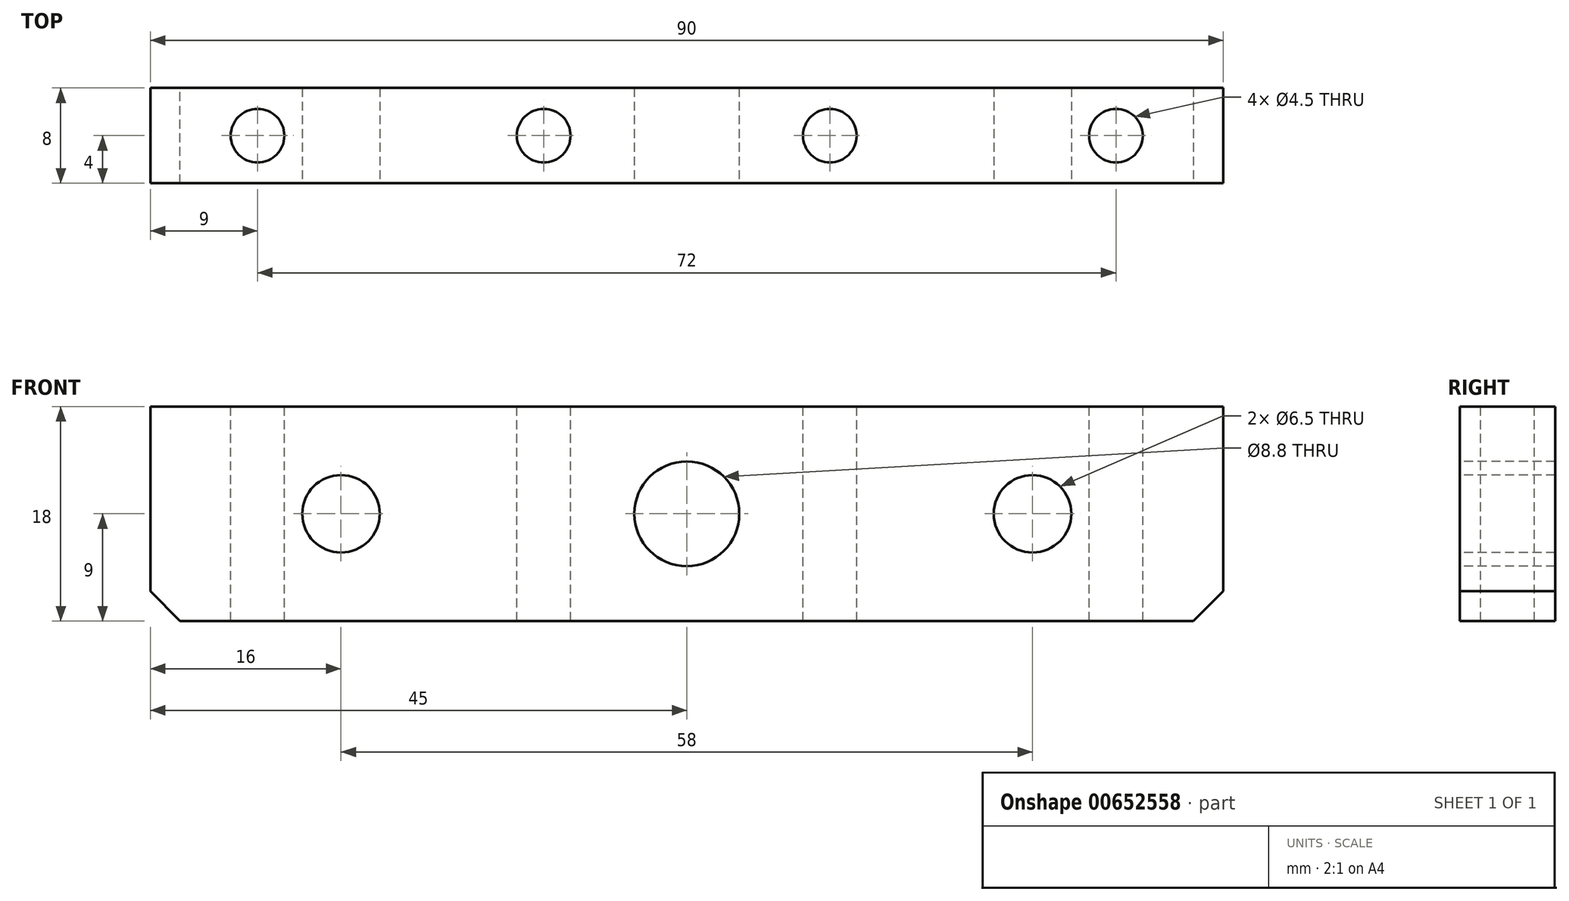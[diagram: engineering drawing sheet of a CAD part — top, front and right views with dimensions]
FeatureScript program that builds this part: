
annotation { "Feature Type Name" : "Feature", "Feature Type Description" : "" }
export const myFeature = defineFeature(function(context is Context, id is Id, definition is map)
    precondition{}
    {
        {
            var Q0;
            Q0=qCreatedBy(makeId("Front.planeOp"),FACE);
            var sketch = newSketch(context, id + "F0", { "sketchPlane" : qUnion([Q0])});
            skLineSegment(sketch, "E0.bottom", {"start": v(45, 9) * mm, "end": v(-45, 9) * mm});
            skLineSegment(sketch, "E0.top", {"start": v(45, -9) * mm, "end": v(-45, -9) * mm});
            skLineSegment(sketch, "E0.left", {"start": v(45, 9) * mm, "end": v(45, -9) * mm});
            skLineSegment(sketch, "E0.right", {"start": v(-45, 9) * mm, "end": v(-45, -9) * mm});
            skPoint(sketch, "E0.middle", {"position": v(0, 0) * mm});
            skSolve(sketch);
        }
        {
            var Q0;
            Q0=makeQuery(id+"F0.imprint","IMPRINT",FACE,{"disambiguationData":[TD([[makeQuery(id+"F0.imprint","IMPRINT",EDGE,{"derivedFrom":sQuery(id+"F0.wireOp",EDGE,"E0.bottom")}),1.0]])]});
            extrude(context, id + "F1", {"entities" : qUnion([Q0]), "depth" : 4 * mm, "offsetDistance" : 25 * mm, "hasSecondDirection" : true, "secondDirectionOppositeDirection" : true, "secondDirectionDepth" : 4 * mm});
        }
        {
            var Q0;
            Q0=makeQuery(id+"F1.opExtrude","SWEPT_EDGE",EDGE,{"disambiguationData":[OSD([sQuery(id+"F0.wireOp",EDGE,"E0.top"),sQuery(id+"F0.wireOp",EDGE,"E0.right")])]});
            var Q1;
            Q1=makeQuery(id+"F1.opExtrude","SWEPT_EDGE",EDGE,{"disambiguationData":[OSD([sQuery(id+"F0.wireOp",EDGE,"E0.top"),sQuery(id+"F0.wireOp",EDGE,"E0.left")])]});
            chamfer(context, id + "F2", {"entities" : qUnion([Q0, Q1]), "width" : 2.5 * mm, "tangentPropagation" : true});
        }
        {
            var Q0;
            Q0=makeQuery(id+"F1.opExtrude","CAP_FACE",FACE,{"disambiguationData":[OSD([sQuery(id+"F0.wireOp",EDGE,"E0.bottom"),sQuery(id+"F0.wireOp",EDGE,"E0.top"),sQuery(id+"F0.wireOp",EDGE,"E0.left"),sQuery(id+"F0.wireOp",EDGE,"E0.right")])],"isStart":false});
            var sketch = newSketch(context, id + "F3", { "sketchPlane" : qUnion([Q0])});
            skPoint(sketch, "E1", {"position": v(-29, 0) * mm});
            skPoint(sketch, "E2", {"position": v(0, 0) * mm});
            skPoint(sketch, "E3", {"position": v(29, 0) * mm});
            skSolve(sketch);
        }
        {
            var Q0;
            Q0=sQuery(id+"F3.wireOp",VERTEX,"E1");
            var Q1;
            Q1=sQuery(id+"F3.wireOp",VERTEX,"E3");
            var Q2;
            Q2=makeQuery(id+"F1.opExtrude","SWEPT_BODY",BODY,{"disambiguationData":[OSD([sQuery(id+"F0.wireOp",EDGE,"E0.bottom"),sQuery(id+"F0.wireOp",EDGE,"E0.top"),sQuery(id+"F0.wireOp",EDGE,"E0.left"),sQuery(id+"F0.wireOp",EDGE,"E0.right")])]});
            hole(context, id + "F4", {"style" : HoleStyle.SIMPLE, "endStyle" : HoleEndStyle.THROUGH, "holeDiameter" : 6.5 * mm, "majorDiameter" : 5 * mm, "isTappedThrough" : true, "tappedDepth" : 12 * mm, "tapClearance" : 3, "locations" : qUnion([Q0, Q1]), "scope" : qUnion([Q2])});
        }
        {
            var Q0;
            Q0=sQuery(id+"F3.wireOp",VERTEX,"E2");
            var Q1;
            Q1=makeQuery(id+"F1.opExtrude","SWEPT_BODY",BODY,{"disambiguationData":[OSD([sQuery(id+"F0.wireOp",EDGE,"E0.bottom"),sQuery(id+"F0.wireOp",EDGE,"E0.top"),sQuery(id+"F0.wireOp",EDGE,"E0.left"),sQuery(id+"F0.wireOp",EDGE,"E0.right")])]});
            hole(context, id + "F5", {"style" : HoleStyle.SIMPLE, "endStyle" : HoleEndStyle.THROUGH, "standardTappedOrClearance" : lookupTablePath({ "standard" : "ISO", "fit" : "Normal", "size" : "M8", "type" : "Clearance" }), "standardBlindInLast" : lookupTablePath({ "fit" : "Standard", "standard" : "ISO", "size" : "M8", "type" : "Clearance" }), "holeDiameter" : 8.8 * mm, "majorDiameter" : 5 * mm, "isTappedThrough" : true, "tappedDepth" : 12 * mm, "tapClearance" : 3, "locations" : qUnion([Q0]), "scope" : qUnion([Q1])});
        }
        {
            var Q0;
            Q0=makeQuery(id+"F1.opExtrude","SWEPT_FACE",FACE,{"disambiguationData":[OSD([sQuery(id+"F0.wireOp",EDGE,"E0.bottom")])]});
            var sketch = newSketch(context, id + "F6", { "sketchPlane" : qUnion([Q0])});
            skPoint(sketch, "E4", {"position": v(-36, 0) * mm});
            skPoint(sketch, "E5", {"position": v(-12, 0) * mm});
            skPoint(sketch, "E6", {"position": v(12, 0) * mm});
            skPoint(sketch, "E7", {"position": v(36, 0) * mm});
            skSolve(sketch);
        }
        {
            var Q0;
            Q0=sQuery(id+"F6.wireOp",VERTEX,"E4");
            var Q1;
            Q1=sQuery(id+"F6.wireOp",VERTEX,"E5");
            var Q2;
            Q2=sQuery(id+"F6.wireOp",VERTEX,"E6");
            var Q3;
            Q3=sQuery(id+"F6.wireOp",VERTEX,"E7");
            var Q4;
            Q4=makeQuery(id+"F1.opExtrude","SWEPT_BODY",BODY,{"disambiguationData":[OSD([sQuery(id+"F0.wireOp",EDGE,"E0.bottom"),sQuery(id+"F0.wireOp",EDGE,"E0.top"),sQuery(id+"F0.wireOp",EDGE,"E0.left"),sQuery(id+"F0.wireOp",EDGE,"E0.right")])]});
            hole(context, id + "F7", {"style" : HoleStyle.SIMPLE, "endStyle" : HoleEndStyle.THROUGH, "holeDiameter" : 4.5 * mm, "majorDiameter" : 5 * mm, "isTappedThrough" : true, "tappedDepth" : 12 * mm, "tapClearance" : 3, "locations" : qUnion([Q0, Q1, Q2, Q3]), "scope" : qUnion([Q4])});
        }
    });
